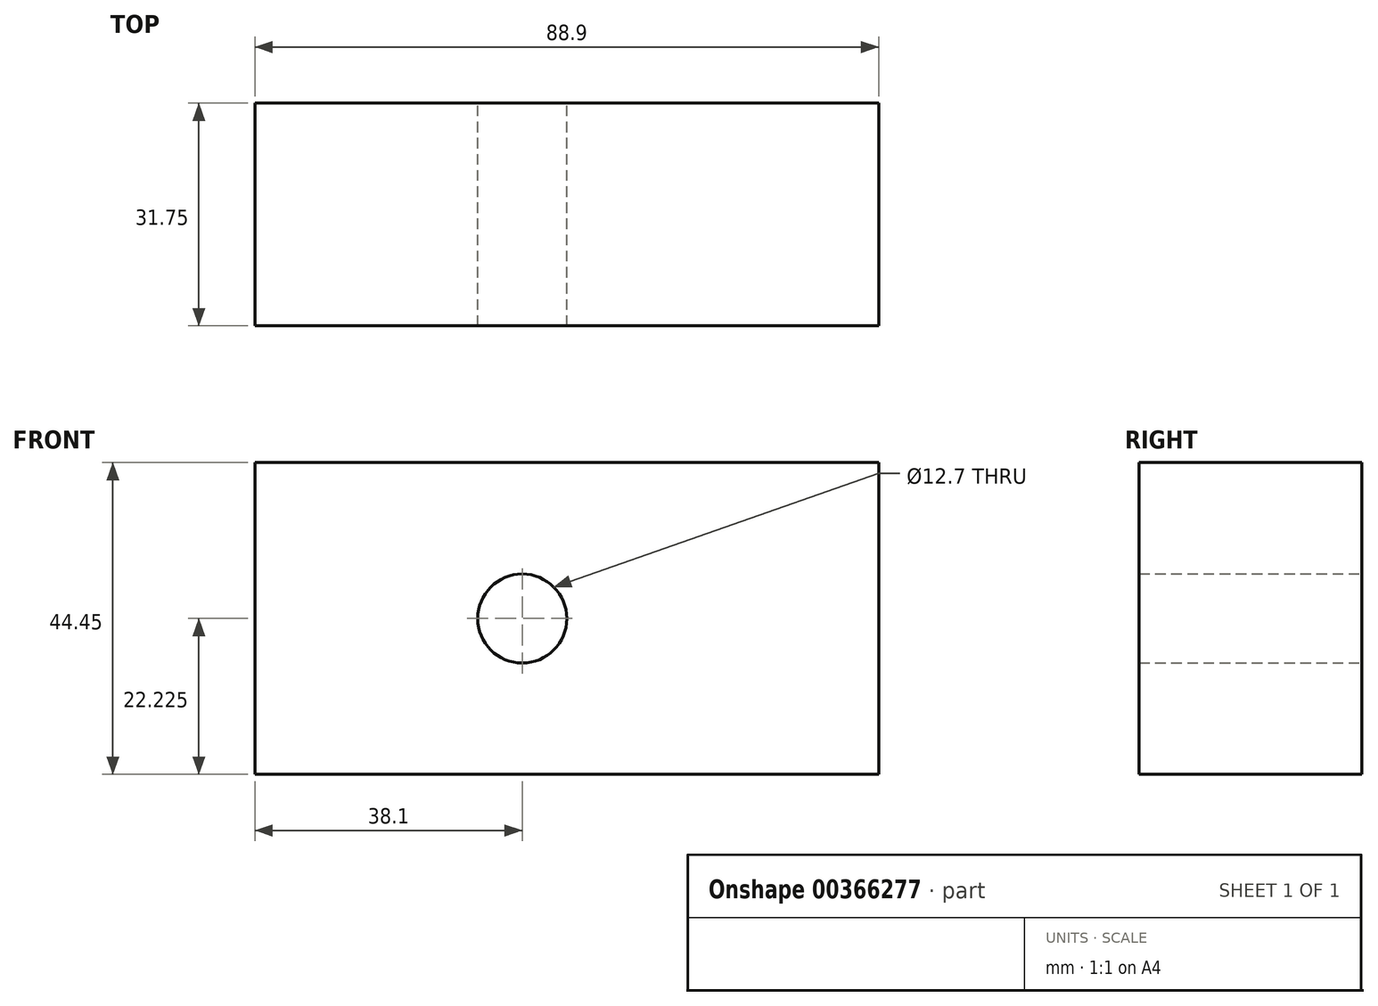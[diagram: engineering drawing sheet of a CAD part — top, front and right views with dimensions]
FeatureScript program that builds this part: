
annotation { "Feature Type Name" : "Feature", "Feature Type Description" : "" }
export const myFeature = defineFeature(function(context is Context, id is Id, definition is map)
    precondition{}
    {
        {
            var Q0;
            Q0=qCreatedBy(makeId("Front.planeOp"),FACE);
            var sketch = newSketch(context, id + "F0", { "sketchPlane" : qUnion([Q0])});
            skLineSegment(sketch, "E0", {"start": v(0, 0) * mm, "end": v(88.9, 0) * mm});
            skLineSegment(sketch, "E1", {"start": v(88.9, 0) * mm, "end": v(88.9, 44.45) * mm});
            skLineSegment(sketch, "E2", {"start": v(88.9, 44.45) * mm, "end": v(0, 44.45) * mm});
            skLineSegment(sketch, "E3", {"start": v(0, 44.45) * mm, "end": v(0, 0) * mm});
            skCircle(sketch, "E4", {"center": v(38.1, 22.22) * mm, "radius": 6.35 * mm});
            skSolve(sketch);
        }
        {
            var Q0;
            Q0 = qSketchRegion(id + "F0", true);
            extrude(context, id + "F1", {"entities" : qUnion([Q0]), "depth" : 31.75 * mm});
        }
    });
